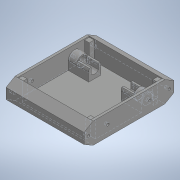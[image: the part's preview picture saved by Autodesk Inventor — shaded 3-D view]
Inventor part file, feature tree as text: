
AUTODESK INVENTOR PART (.ipt)
format: ipt  version: 2020 (Build 240168000, 168)  size: 266,240 bytes
history: native  units: in
note: dims shown in document units (in); Inventor stores cm internally (conversion verified against a paired STEP export)
features: extrude x8, sketch x8, projected_geometry x4, mirror x3
ambient origin geometry x8: Origin, YZ Plane, XZ Plane, XY Plane, X Axis, Y Axis, Z Axis, Center Point
bodies: Solid1 (feature_tree)
feature tree (23):
  extrude  "Extrusion1"  Depth=5.9055in
  extrude  "Extrusion2"  TaperAngle=0.0deg  [1 undecoded]
  extrude  "Extrusion3"  Depth=1.2598in
  extrude  "Extrusion4"  Depth=0.315in
  extrude  "Extrusion5"  TaperAngle=0.0deg  [1 undecoded]
  extrude  "Extrusion6"  Depth=0.689in
  mirror  "Mirror1"
  extrude  "Extrusion7"  Depth=0.0787in
  mirror  "Mirror2"
  extrude  "Extrusion8"  Depth=0.2756in
  mirror  "Mirror3"
  sketch  "Sketch1"  dims[d0=1.378in d1=5.9055in]
  sketch  "Sketch2"  dims[d2=5.1181in d3=0.0in]
  projected_geometry  "Projected Loop1"
  sketch  "Sketch3"  dims[d4=0.1575in d5=1.2598in]
  projected_geometry  "Projected Loop2"
  projected_geometry  "Projected Loop3"
  sketch  "Sketch4"  dims[d6=0.0in d8=0.315in]
  sketch  "Sketch5"  dims[d10=1.1898in d11=0.0in]
  projected_geometry  "Projected Loop4"
  sketch  "Sketch6"  dims[d12=0.6496in d13=0.689in]
  sketch  "Sketch7"  dims[d14=1.5748in d15=0.0787in]
  sketch  "Sketch9"  dims[d16=0.5512in d17=0.0in d18=0.6102in d19=0.4803in d20=0.7874in d21=0.0in d22=0.1654in d23=6.063in d24=0.0in d25=0.5967in d26=0.1575in d27=1.5748in d28=0.0in d29=0.0in d30=0.1575in d31=0.2756in d32=0.0in]
note: 2 required parameter values undecoded (feature->parameter linkage not recoverable at this tier; creation-order binding heuristic only, values carry confidence <= 0.55)
